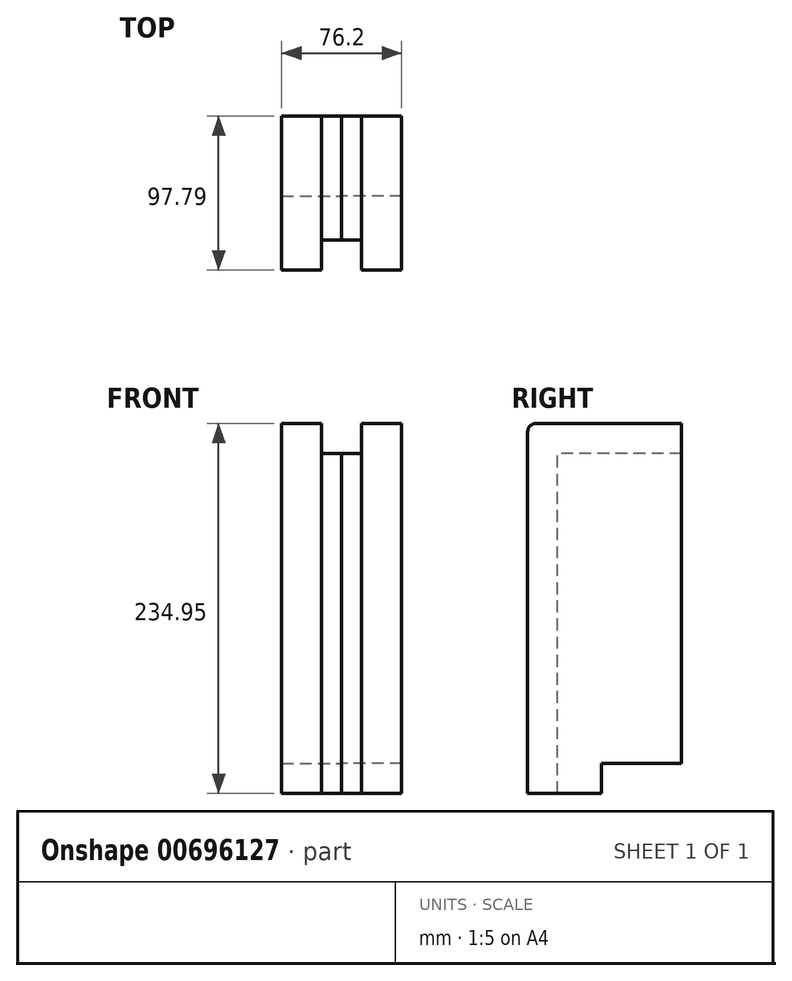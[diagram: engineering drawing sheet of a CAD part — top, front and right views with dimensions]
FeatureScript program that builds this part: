
annotation { "Feature Type Name" : "Feature", "Feature Type Description" : "" }
export const myFeature = defineFeature(function(context is Context, id is Id, definition is map)
    precondition{}
    {
        {
            var Q0;
            Q0=qCreatedBy(makeId("Right.planeOp"),FACE);
            var sketch = newSketch(context, id + "F0", { "sketchPlane" : qUnion([Q0])});
            skLineSegment(sketch, "E0.bottom", {"start": v(97.8, -19.05) * mm, "end": v(0, -19.05) * mm});
            skLineSegment(sketch, "E0.top", {"start": v(97.8, -254) * mm, "end": v(0, -254) * mm});
            skLineSegment(sketch, "E0.left", {"start": v(97.8, -19.05) * mm, "end": v(97.8, -254) * mm});
            skLineSegment(sketch, "E0.right", {"start": v(0, -19.05) * mm, "end": v(0, -254) * mm});
            skSolve(sketch);
        }
        {
            var Q0;
            Q0=makeQuery(id+"F0.imprint","IMPRINT",FACE,{"disambiguationData":[TD([[makeQuery(id+"F0.imprint","IMPRINT",EDGE,{"derivedFrom":sQuery(id+"F0.wireOp",EDGE,"E0.bottom")}),1.0]])]});
            extrude(context, id + "F1", {"entities" : qUnion([Q0]), "depth" : 38.1 * mm, "offsetDistance" : 25.4 * mm});
        }
        {
            var Q0;
            Q0=makeQuery(id+"F1.opExtrude","CAP_FACE",FACE,{"disambiguationData":[OSD([sQuery(id+"F0.wireOp",EDGE,"E0.bottom"),sQuery(id+"F0.wireOp",EDGE,"E0.top"),sQuery(id+"F0.wireOp",EDGE,"E0.left"),sQuery(id+"F0.wireOp",EDGE,"E0.right")])],"isStart":true});
            var sketch = newSketch(context, id + "F2", { "sketchPlane" : qUnion([Q0])});
            skLineSegment(sketch, "E1.bottom", {"start": v(-97.8, -19.05) * mm, "end": v(0, -19.05) * mm});
            skLineSegment(sketch, "E1.top", {"start": v(-97.8, -38.1) * mm, "end": v(0, -38.1) * mm});
            skLineSegment(sketch, "E1.left", {"start": v(-97.8, -19.05) * mm, "end": v(-97.8, -38.1) * mm});
            skLineSegment(sketch, "E1.right", {"start": v(0, -19.05) * mm, "end": v(0, -38.1) * mm});
            skLineSegment(sketch, "E2.bottom", {"start": v(0, -254) * mm, "end": v(-19.05, -254) * mm});
            skLineSegment(sketch, "E2.top", {"start": v(0, -19.05) * mm, "end": v(-19.05, -19.05) * mm});
            skLineSegment(sketch, "E2.left", {"start": v(0, -254) * mm, "end": v(0, -19.05) * mm});
            skLineSegment(sketch, "E2.right", {"start": v(-19.05, -254) * mm, "end": v(-19.05, -19.05) * mm});
            skLineSegment(sketch, "E3.bottom", {"start": v(-97.8, -254) * mm, "end": v(-47, -254) * mm});
            skLineSegment(sketch, "E3.top", {"start": v(-97.8, -234.95) * mm, "end": v(-47, -234.95) * mm});
            skLineSegment(sketch, "E3.left", {"start": v(-97.8, -254) * mm, "end": v(-97.8, -234.95) * mm});
            skLineSegment(sketch, "E3.right", {"start": v(-47, -254) * mm, "end": v(-47, -234.95) * mm});
            skSolve(sketch);
        }
        {
            var Q0;
            {var subQ5=sQuery(id+"F2.wireOp",EDGE,"E2.bottom");Q0=makeQuery(id+"F2.imprint","IMPRINT",FACE,{"disambiguationData":[TD([[makeQuery(id+"F2.imprint","IMPRINT",EDGE,{"derivedFrom":subQ5}),1.0]])]});}
            var Q1;
            {var subQ5=sQuery(id+"F2.wireOp",EDGE,"E2.top");Q1=makeQuery(id+"F2.imprint","IMPRINT",FACE,{"disambiguationData":[TD([[makeQuery(id+"F2.imprint","IMPRINT",EDGE,{"derivedFrom":subQ5}),-1.0]])]});}
            var Q2;
            {var subQ0=sQuery(id+"F2.wireOp",EDGE,"E1.bottom");Q2=makeQuery(id+"F2.imprint","IMPRINT",FACE,{"disambiguationData":[TD([[makeQuery(id+"F2.imprint","IMPRINT",EDGE,{"derivedFrom":subQ0}),-1.0]])]});}
            extrude(context, id + "F3", {"entities" : qUnion([Q0, Q1, Q2]), "operationType" : NewBodyOperationType.REMOVE, "oppositeDirection" : true, "depth" : 12.7 * mm, "offsetDistance" : 25.4 * mm});
        }
        {
            var Q0;
            Q0=makeQuery(id+"F2.imprint","IMPRINT",FACE,{"disambiguationData":[TD([[makeQuery(id+"F2.imprint","IMPRINT",EDGE,{"derivedFrom":sQuery(id+"F2.wireOp",EDGE,"E3.bottom")}),1.0]])]});
            extrude(context, id + "F4", {"entities" : qUnion([Q0]), "operationType" : NewBodyOperationType.REMOVE, "endBound" : BoundingType.THROUGH_ALL, "oppositeDirection" : true, "depth" : 25.4 * mm, "offsetDistance" : 25.4 * mm});
        }
        {
            var Q0;
            Q0=makeQuery(id+"F1.opExtrude","SWEPT_EDGE",EDGE,{"disambiguationData":[OSD([sQuery(id+"F0.wireOp",EDGE,"E0.bottom"),sQuery(id+"F0.wireOp",EDGE,"E0.right")])]});
            fillet(context, id + "F5", {"entities" : qUnion([Q0]), "radius" : 5.08 * mm, "allowEdgeOverflow" : false});
        }
        {
            var Q0;
            Q0=makeQuery(id+"F1.opExtrude","SWEPT_BODY",BODY,{"disambiguationData":[OSD([sQuery(id+"F0.wireOp",EDGE,"E0.bottom"),sQuery(id+"F0.wireOp",EDGE,"E0.top"),sQuery(id+"F0.wireOp",EDGE,"E0.left"),sQuery(id+"F0.wireOp",EDGE,"E0.right")])]});
            var Q1;
            Q1=qCreatedBy(makeId("Right.planeOp"),FACE);
            mirror(context, id + "F6", {"entities" : qUnion([Q0]), "mirrorPlane" : qUnion([Q1])});
        }
    });
